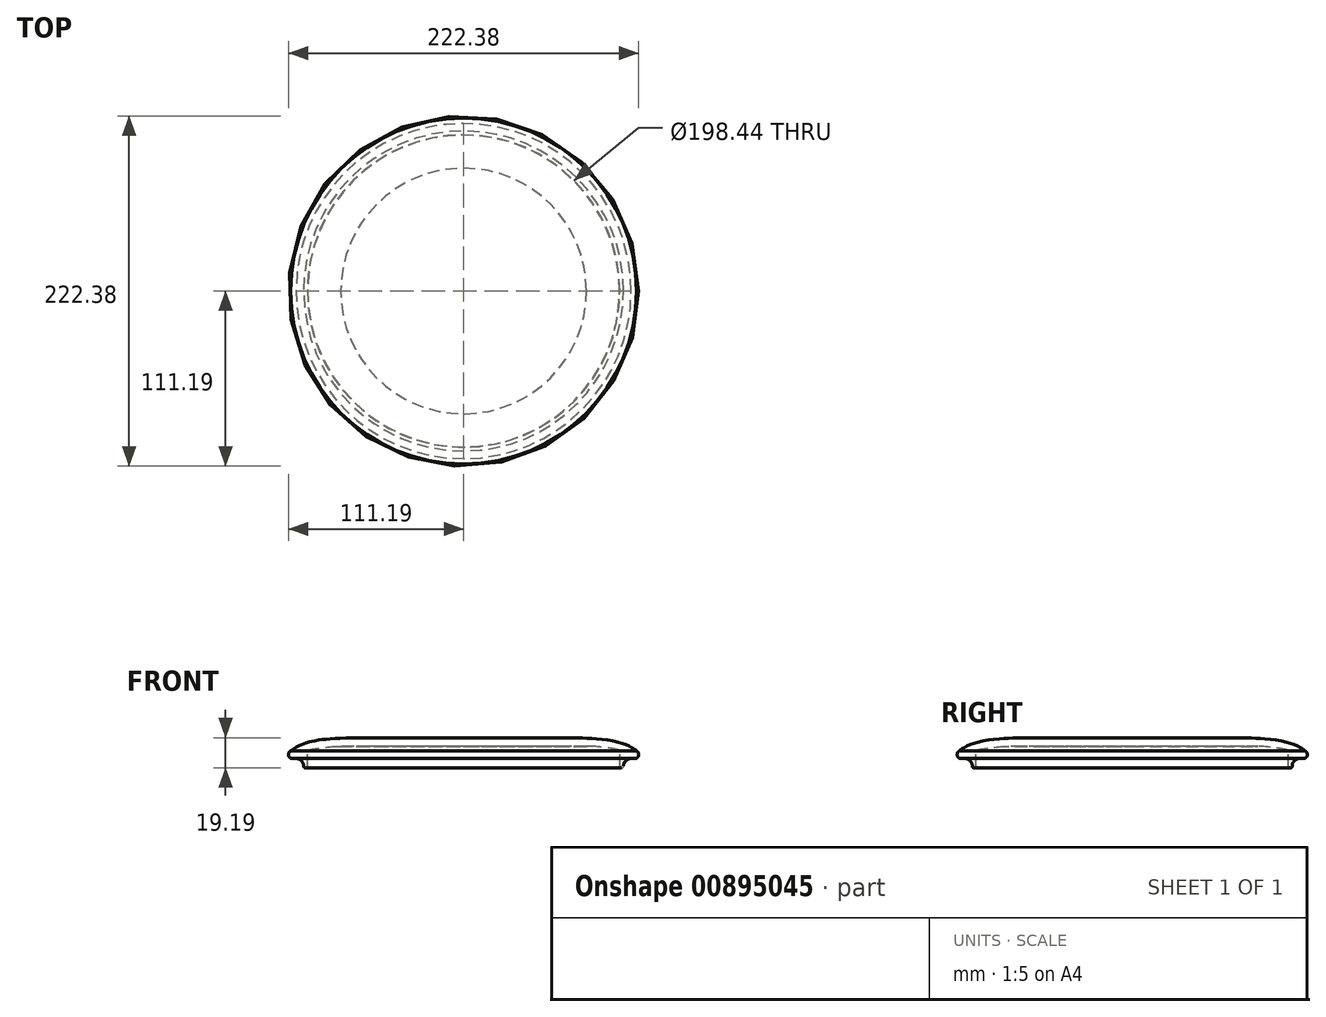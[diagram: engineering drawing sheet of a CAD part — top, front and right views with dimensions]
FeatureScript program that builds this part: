
annotation { "Feature Type Name" : "Feature", "Feature Type Description" : "" }
export const myFeature = defineFeature(function(context is Context, id is Id, definition is map)
    precondition{}
    {
        {
            var Q0;
            Q0=qCreatedBy(makeId("Front.planeOp"),FACE);
            var sketch = newSketch(context, id + "F0", { "sketchPlane" : qUnion([Q0])});
            skPoint(sketch, "E0", {"position": v(-99.22, 0) * mm});
            skPoint(sketch, "E1", {"position": v(0, 0) * mm});
            skPoint(sketch, "E2", {"position": v(-101.6, 0) * mm});
            skPoint(sketch, "E3", {"position": v(-99.22, 9.6) * mm});
            skPoint(sketch, "E4", {"position": v(-100.4, -1.2) * mm});
            skArc(sketch, "E5", {"start": v(-101.6, 0) * mm, "mid": v(-100.4, -1.2) * mm, "end": v(-99.22, 0) * mm});
            skPoint(sketch, "E6", {"position": v(-106.44, 4.76) * mm});
            skArc(sketch, "E7", {"start": v(-101.6, 0) * mm, "mid": v(-103.02, 3.4) * mm, "end": v(-106.44, 4.76) * mm});
            skPoint(sketch, "E8", {"position": v(-108.81, 4.78) * mm});
            skLineSegment(sketch, "E9", {"start": v(-106.44, 4.76) * mm, "end": v(-108.81, 4.78) * mm});
            skPoint(sketch, "E10", {"position": v(-111.2, 7.16) * mm});
            skArc(sketch, "E11", {"start": v(-108.81, 4.78) * mm, "mid": v(-110.5, 5.48) * mm, "end": v(-111.2, 7.16) * mm});
            skPoint(sketch, "E12", {"position": v(-81.03, 17.48) * mm});
            skPoint(sketch, "E13", {"position": v(-106.43, 11.92) * mm});
            skPoint(sketch, "E14", {"position": v(-98.5, 15.1) * mm});
            skPoint(sketch, "E15", {"position": v(-108.16, 7.17) * mm});
            skArc(sketch, "E16", {"start": v(-111.2, 7.16) * mm, "mid": v(-110.85, 8.58) * mm, "end": v(-109.87, 9.67) * mm});
            skPoint(sketch, "E17", {"position": v(0, 17.48) * mm});
            skFitSpline(sketch, "E18", {"points": [v(-109.87, 9.67) * mm, v(-106.43, 11.92) * mm, v(-98.5, 15.1) * mm, v(-81.03, 17.48) * mm, v(0, 17.48) * mm], "startDerivative": vector(31.7, 18.76) * mm, "endDerivative": vector(194.12, -2.74) * mm});
            skLineSegment(sketch, "E19", {"start": v(-99.22, 9.6) * mm, "end": v(-99.22, 0) * mm});
            skPoint(sketch, "E20", {"position": v(-81.03, 12.48) * mm});
            skPoint(sketch, "E21", {"position": v(0, 12.44) * mm});
            skPoint(sketch, "E22", {"position": v(-98.82, 9.6) * mm});
            skPoint(sketch, "E23", {"position": v(-59.84, 12.48) * mm});
            skLineSegment(sketch, "E24", {"start": v(0, 12.44) * mm, "end": v(-59.84, 12.48) * mm});
            skPoint(sketch, "E25", {"position": v(-93.36, 16.26) * mm});
            skPoint(sketch, "E26", {"position": v(-93.36, 11.26) * mm});
            skPoint(sketch, "E27", {"position": v(-97.14, 15.46) * mm});
            skPoint(sketch, "E28", {"position": v(-97.14, 10.46) * mm});
            skLineSegment(sketch, "E29", {"start": v(-59.84, 12.48) * mm, "end": v(-77.98, 12.48) * mm});
            skArc(sketch, "E30", {"start": v(-99.22, 9.6) * mm, "mid": v(-99.17, 9.78) * mm, "end": v(-99.05, 9.92) * mm});
            skFitSpline(sketch, "E31", {"points": [v(-99.05, 9.92) * mm, v(-97.14, 10.46) * mm, v(-93.36, 11.26) * mm, v(-81.03, 12.48) * mm, v(-77.98, 12.48) * mm], "startDerivative": vector(11.4, 4.6) * mm, "endDerivative": vector(11.7, 0.3) * mm});
            skLineSegment(sketch, "E32", {"start": v(0, 17.48) * mm, "end": v(0, 12.44) * mm});
            skSolve(sketch);
        }
        {
            var Q0;
            Q0=makeQuery(id+"F0.imprint","IMPRINT",FACE,{"disambiguationData":[TD([[makeQuery(id+"F0.imprint","IMPRINT",EDGE,{"derivedFrom":sQuery(id+"F0.wireOp",EDGE,"E5")}),1.0]])]});
            var Q1;
            Q1=sQuery(id+"F0.wireOp",EDGE,"E32");
            revolve(context, id + "F1", {"surfaceOperationType" : NewSurfaceOperationType.NEW, "entities" : qUnion([Q0]), "axis" : qUnion([Q1]), "revolveType" : RevolveType.FULL});
        }
    });
